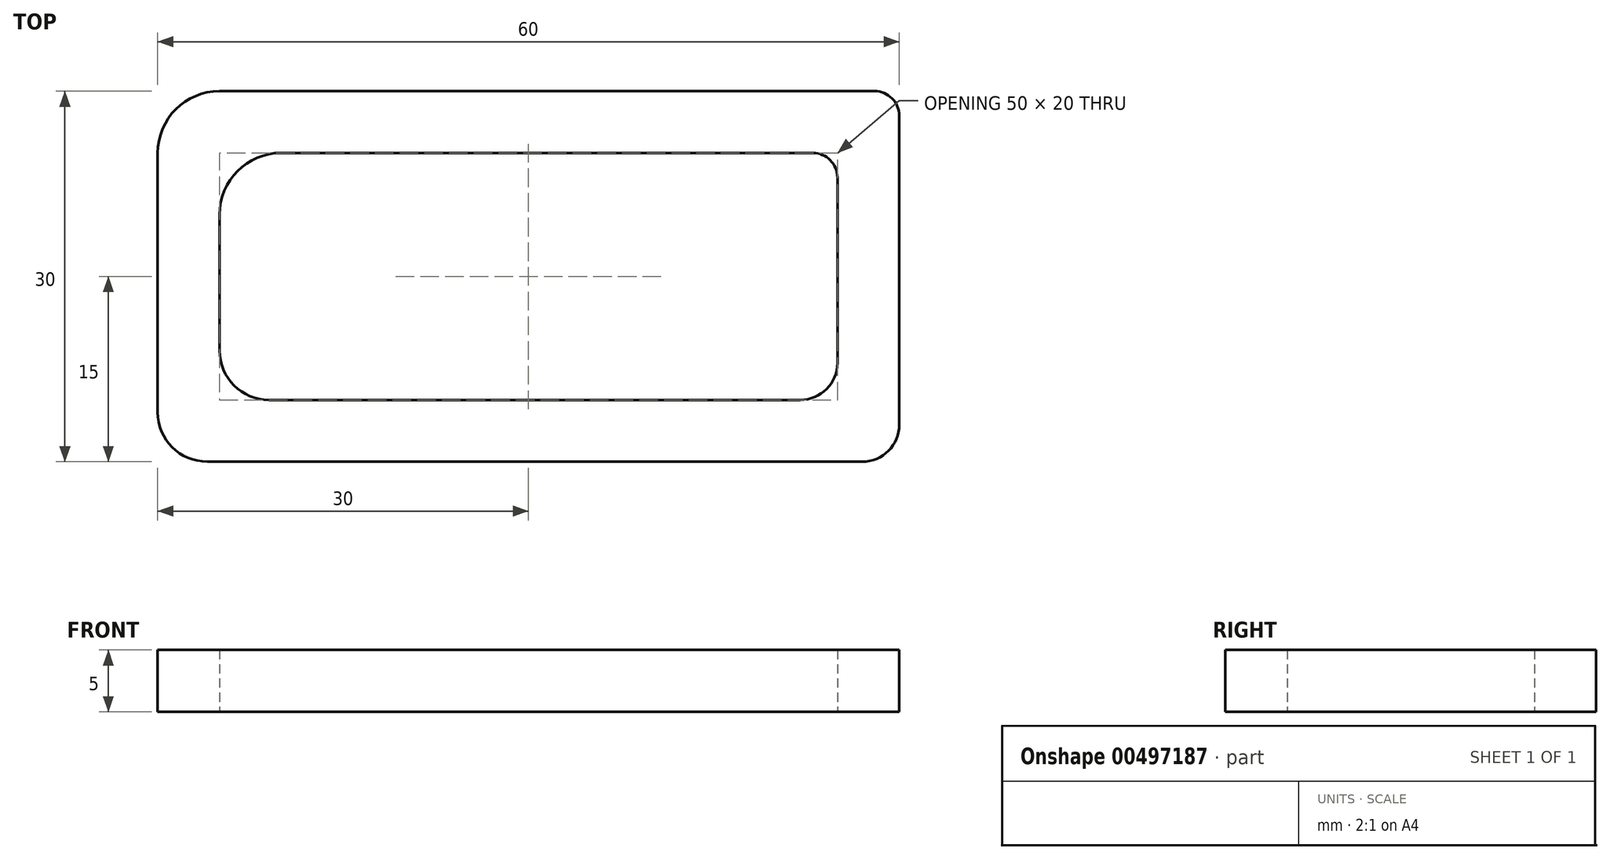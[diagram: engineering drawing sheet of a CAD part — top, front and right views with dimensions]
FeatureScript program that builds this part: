
annotation { "Feature Type Name" : "Feature", "Feature Type Description" : "" }
export const myFeature = defineFeature(function(context is Context, id is Id, definition is map)
    precondition{}
    {
        {
            var Q0;
            Q0=qCreatedBy(makeId("Top.planeOp"),FACE);
            var sketch = newSketch(context, id + "F0", { "sketchPlane" : qUnion([Q0])});
            skLineSegment(sketch, "E0.bottom", {"start": v(-25, 15) * mm, "end": v(28, 15) * mm});
            skLineSegment(sketch, "E0.top", {"start": v(-26, -15) * mm, "end": v(27, -15) * mm});
            skLineSegment(sketch, "E0.left", {"start": v(-30, 10) * mm, "end": v(-30, -11) * mm});
            skLineSegment(sketch, "E0.right", {"start": v(30, 13) * mm, "end": v(30, -12) * mm});
            skPoint(sketch, "E0.middle", {"position": v(0, 0) * mm});
            skLineSegment(sketch, "E1.bottom", {"start": v(-20, 10) * mm, "end": v(23, 10) * mm});
            skLineSegment(sketch, "E1.top", {"start": v(-21, -10) * mm, "end": v(22, -10) * mm});
            skLineSegment(sketch, "E1.left", {"start": v(-25, 5) * mm, "end": v(-25, -6) * mm});
            skLineSegment(sketch, "E1.right", {"start": v(25, 8) * mm, "end": v(25, -7) * mm});
            skPoint(sketch, "E2.visualSharp", {"position": v(-25, 10) * mm});
            skArc(sketch, "E2.filletArc", {"start": v(-20, 10) * mm, "mid": v(-23.54, 8.54) * mm, "end": v(-25, 5) * mm});
            skPoint(sketch, "E3.visualSharp", {"position": v(-25, -10) * mm});
            skArc(sketch, "E3.filletArc", {"start": v(-25, -6) * mm, "mid": v(-23.83, -8.83) * mm, "end": v(-21, -10) * mm});
            skPoint(sketch, "E4.visualSharp", {"position": v(25, -10) * mm});
            skArc(sketch, "E4.filletArc", {"start": v(22, -10) * mm, "mid": v(24.12, -9.12) * mm, "end": v(25, -7) * mm});
            skPoint(sketch, "E5.visualSharp", {"position": v(25, 10) * mm});
            skArc(sketch, "E5.filletArc", {"start": v(25, 8) * mm, "mid": v(24.41, 9.41) * mm, "end": v(23, 10) * mm});
            skPoint(sketch, "E6.visualSharp", {"position": v(30, 15) * mm});
            skArc(sketch, "E6.filletArc", {"start": v(30, 13) * mm, "mid": v(29.41, 14.41) * mm, "end": v(28, 15) * mm});
            skPoint(sketch, "E7.visualSharp", {"position": v(30, -15) * mm});
            skArc(sketch, "E7.filletArc", {"start": v(27, -15) * mm, "mid": v(29.12, -14.12) * mm, "end": v(30, -12) * mm});
            skPoint(sketch, "E8.visualSharp", {"position": v(-30, -15) * mm});
            skArc(sketch, "E8.filletArc", {"start": v(-30, -11) * mm, "mid": v(-28.83, -13.83) * mm, "end": v(-26, -15) * mm});
            skPoint(sketch, "E9.visualSharp", {"position": v(-30, 15) * mm});
            skArc(sketch, "E9.filletArc", {"start": v(-25, 15) * mm, "mid": v(-28.54, 13.54) * mm, "end": v(-30, 10) * mm});
            skSolve(sketch);
        }
        {
            var Q0;
            Q0=makeQuery(id+"F0.imprint","IMPRINT",FACE,{"disambiguationData":[TD([[makeQuery(id+"F0.imprint","IMPRINT",EDGE,{"derivedFrom":sQuery(id+"F0.wireOp",EDGE,"E0.bottom")}),-1.0]])]});
            extrude(context, id + "F1", {"entities" : qUnion([Q0]), "depth" : 5 * mm, "offsetDistance" : 25 * mm});
        }
    });
